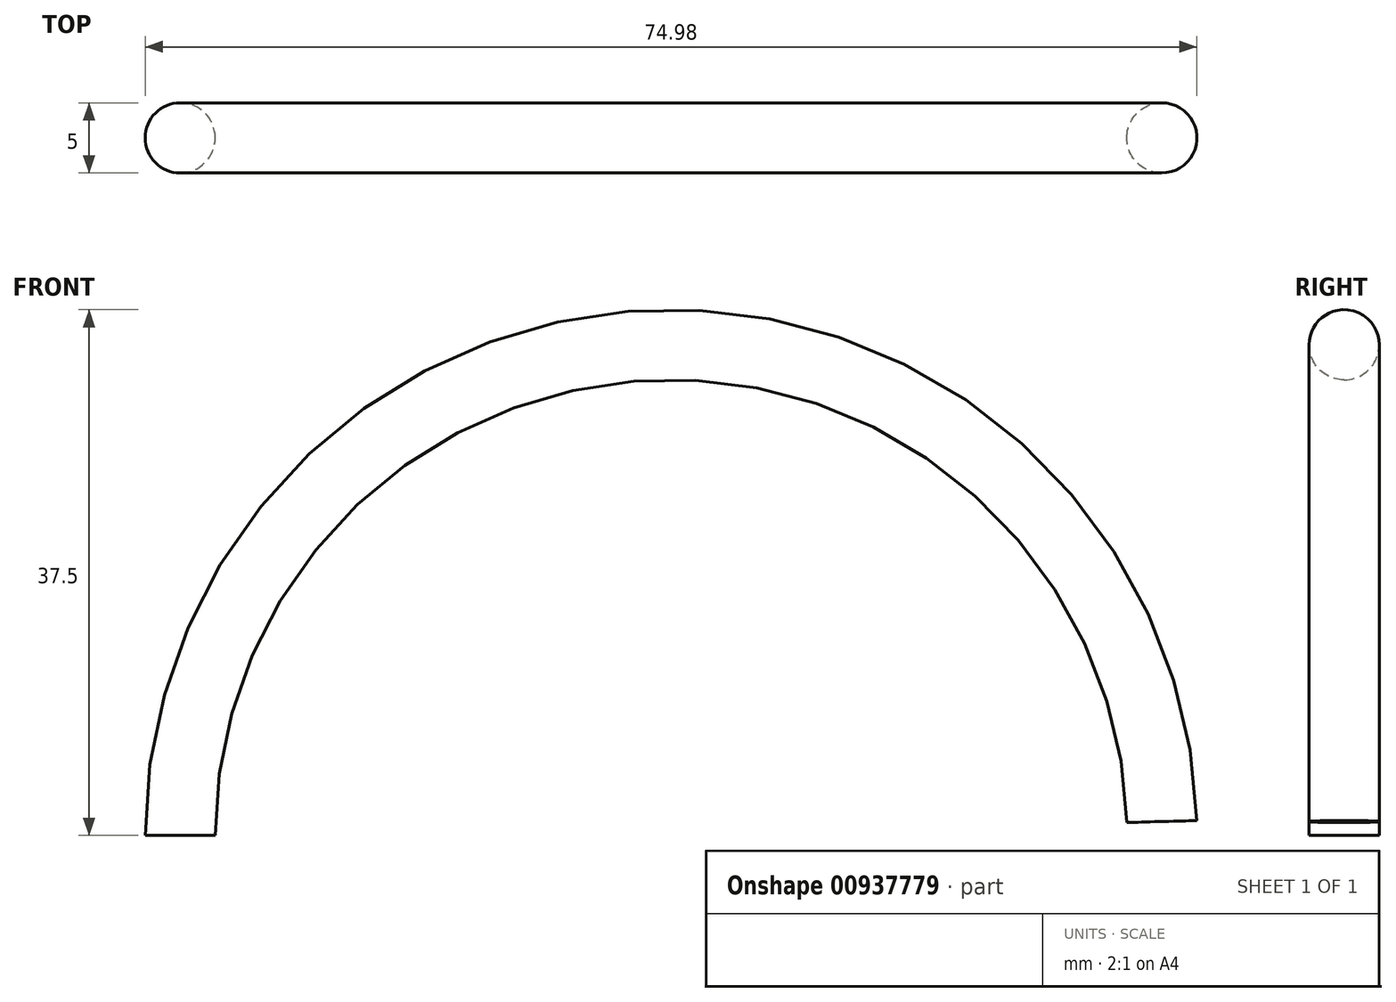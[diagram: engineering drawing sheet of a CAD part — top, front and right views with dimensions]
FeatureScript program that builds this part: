
annotation { "Feature Type Name" : "Feature", "Feature Type Description" : "" }
export const myFeature = defineFeature(function(context is Context, id is Id, definition is map)
    precondition{}
    {
        {
            var Q0;
            Q0=qCreatedBy(makeId("Front.planeOp"),FACE);
            var sketch = newSketch(context, id + "F0", { "sketchPlane" : qUnion([Q0])});
            skArc(sketch, "E0", {"start": v(34.99, 1) * mm, "mid": v(-0.5, 35) * mm, "end": v(-35, 0) * mm});
            skPoint(sketch, "E1", {"position": v(-35, 0) * mm});
            skPoint(sketch, "E2", {"position": v(25.64, -23.82) * mm});
            skLineSegment(sketch, "E3", {"start": v(0, 0) * mm, "end": v(35, 0.79) * mm});
            skLineSegment(sketch, "E4", {"start": v(0, 0) * mm, "end": v(34.99, 1) * mm});
            skSolve(sketch);
        }
        {
            var Q0;
            Q0=qCreatedBy(makeId("Top.planeOp"),FACE);
            var sketch = newSketch(context, id + "F1", { "sketchPlane" : qUnion([Q0])});
            skCircle(sketch, "E5", {"center": v(-35, 0) * mm, "radius": 2.5 * mm});
            skSolve(sketch);
        }
        {
            var Q0;
            Q0=makeQuery(id+"F1.imprint","IMPRINT",FACE,{"disambiguationData":[TD([[makeQuery(id+"F1.imprint","IMPRINT",EDGE,{"derivedFrom":sQuery(id+"F1.wireOp",EDGE,"E5")}),1.0]])]});
            var Q1;
            Q1=sQuery(id+"F0.wireOp",EDGE,"E0");
            sweep(context, id + "F2", {"profiles" : qUnion([Q0]), "path" : qUnion([Q1])});
        }
    });
